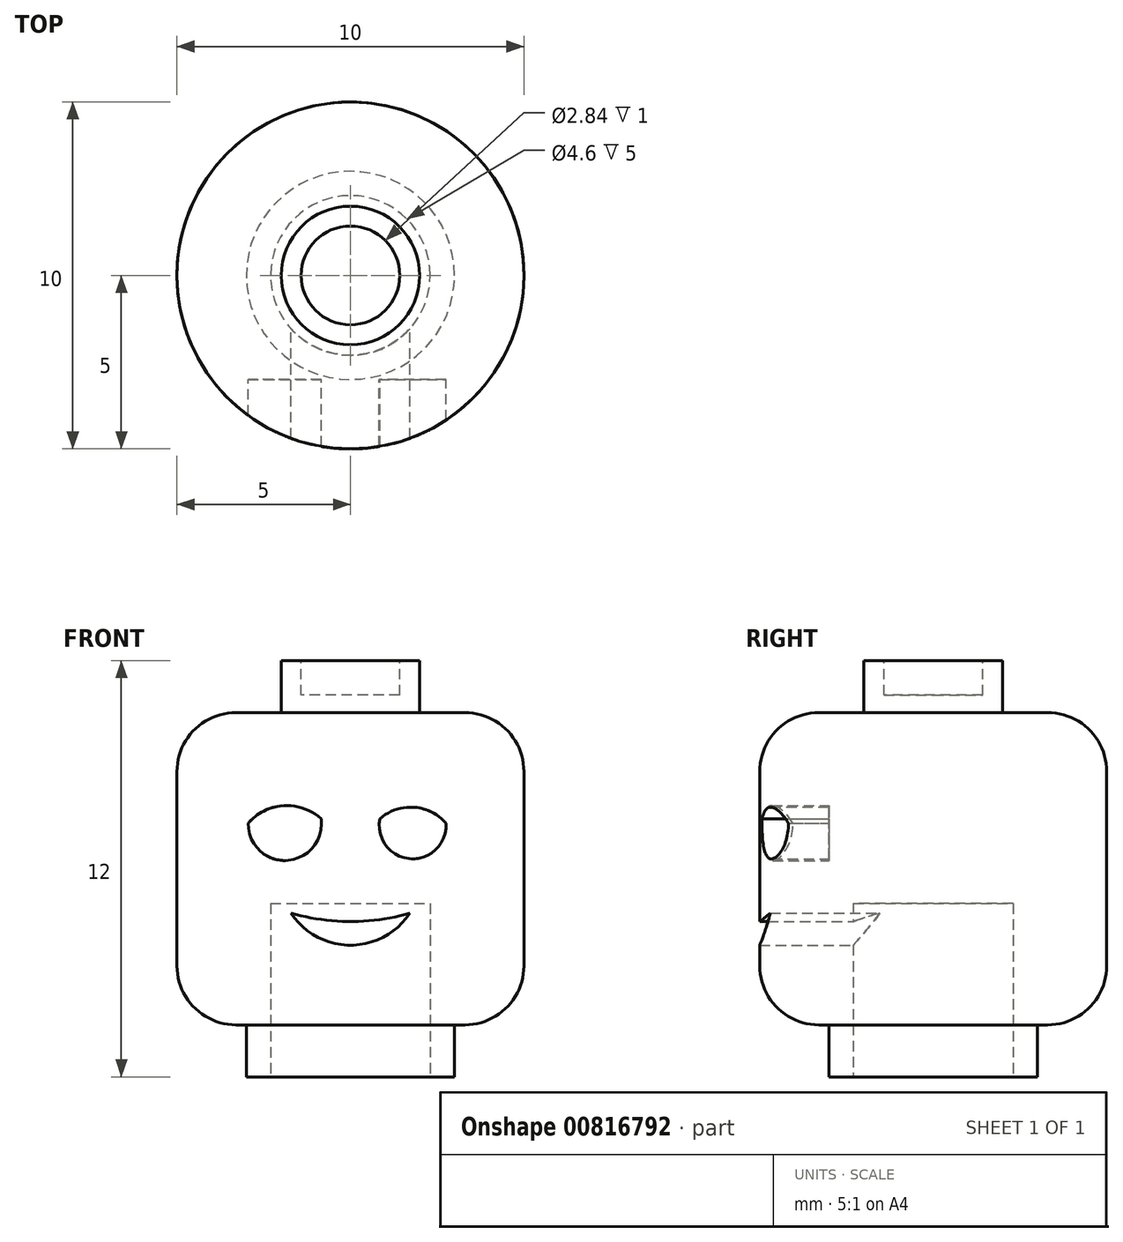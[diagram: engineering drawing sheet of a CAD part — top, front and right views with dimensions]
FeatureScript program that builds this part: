
annotation { "Feature Type Name" : "Feature", "Feature Type Description" : "" }
export const myFeature = defineFeature(function(context is Context, id is Id, definition is map)
    precondition{}
    {
        {
            var Q0;
            Q0=qCreatedBy(makeId("Top.planeOp"),FACE);
            var sketch = newSketch(context, id + "F0", { "sketchPlane" : qUnion([Q0])});
            skCircle(sketch, "E0", {"center": v(0, 0) * mm, "radius": 3 * mm});
            skSolve(sketch);
        }
        {
            var Q0;
            Q0 = qSketchRegion(id + "F0", true);
            extrude(context, id + "F1", {"entities" : qUnion([Q0]), "oppositeDirection" : true, "depth" : 12 * mm, "offsetDistance" : 25 * mm});
        }
        {
            var Q0;
            Q0=makeQuery(id+"F1.opExtrude","CAP_FACE",FACE,{"disambiguationData":[OSD([sQuery(id+"F0.wireOp",EDGE,"E0")])],"isStart":true});
            var sketch = newSketch(context, id + "F2", { "sketchPlane" : qUnion([Q0])});
            skCircle(sketch, "E1", {"center": v(0, 0) * mm, "radius": 2 * mm});
            skCircle(sketch, "E2", {"center": v(0, 0) * mm, "radius": 3.2 * mm});
            skSolve(sketch);
        }
        {
            var Q0;
            Q0 = qSketchRegion(id + "F2", true);
            extrude(context, id + "F3", {"entities" : qUnion([Q0]), "operationType" : NewBodyOperationType.REMOVE, "oppositeDirection" : true, "depth" : 1.5 * mm, "offsetDistance" : 25 * mm});
        }
        {
            var Q0;
            Q0=makeQuery(id+"F3.boolean.opBoolean","COPY",FACE,{"derivedFrom":makeQuery(id+"F3.opExtrude","CAP_FACE",FACE,{"disambiguationData":[OSD([sQuery(id+"F2.wireOp",EDGE,"E1"),sQuery(id+"F2.wireOp",EDGE,"E2")])],"isStart":false})});
            var sketch = newSketch(context, id + "F4", { "sketchPlane" : qUnion([Q0])});
            skCircle(sketch, "E3", {"center": v(0, 0) * mm, "radius": 5 * mm});
            skSolve(sketch);
        }
        {
            var Q0;
            Q0 = qSketchRegion(id + "F4", true);
            extrude(context, id + "F5", {"entities" : qUnion([Q0]), "operationType" : NewBodyOperationType.ADD, "oppositeDirection" : true, "depth" : 9 * mm, "offsetDistance" : 25 * mm});
        }
        {
            var Q0;
            Q0=makeQuery(id+"F5.opExtrude","SWEPT_FACE",FACE,{"disambiguationData":[OSD([sQuery(id+"F4.wireOp",EDGE,"E3")])]});
            fillet(context, id + "F6", {"entities" : qUnion([Q0]), "radius" : 1.7 * mm, "tangentPropagation" : true, "allowEdgeOverflow" : false});
        }
        {
            var Q0;
            Q0=makeQuery(id+"F1.opExtrude","CAP_FACE",FACE,{"disambiguationData":[OSD([sQuery(id+"F0.wireOp",EDGE,"E0")])],"isStart":true});
            var sketch = newSketch(context, id + "F7", { "sketchPlane" : qUnion([Q0])});
            skCircle(sketch, "E4", {"center": v(0, 0) * mm, "radius": 1.42 * mm});
            skSolve(sketch);
        }
        {
            var Q0;
            Q0 = qSketchRegion(id + "F7", true);
            extrude(context, id + "F8", {"entities" : qUnion([Q0]), "operationType" : NewBodyOperationType.REMOVE, "oppositeDirection" : true, "depth" : 1 * mm, "offsetDistance" : 25 * mm});
        }
        {
            var Q0;
            Q0=makeQuery(id+"F1.opExtrude","CAP_FACE",FACE,{"disambiguationData":[OSD([sQuery(id+"F0.wireOp",EDGE,"E0")])],"isStart":false});
            var sketch = newSketch(context, id + "F9", { "sketchPlane" : qUnion([Q0])});
            skCircle(sketch, "E5", {"center": v(0, 0) * mm, "radius": 2.3 * mm});
            skSolve(sketch);
        }
        {
            var Q0;
            Q0 = qSketchRegion(id + "F9", true);
            extrude(context, id + "F10", {"entities" : qUnion([Q0]), "operationType" : NewBodyOperationType.REMOVE, "oppositeDirection" : true, "depth" : 5 * mm, "offsetDistance" : 25 * mm});
        }
        {
            var Q0;
            Q0=qCreatedBy(makeId("Front.planeOp"),FACE);
            var sketch = newSketch(context, id + "F11", { "sketchPlane" : qUnion([Q0])});
            skArc(sketch, "E6", {"start": v(-1.72, -7.28) * mm, "mid": v(0, -8.2) * mm, "end": v(1.7, -7.28) * mm});
            skArc(sketch, "E7", {"start": v(-1.72, -7.28) * mm, "mid": v(0, -7.52) * mm, "end": v(1.7, -7.28) * mm});
            skArc(sketch, "E8", {"start": v(-0.84, -4.56) * mm, "mid": v(-1.92, -4.18) * mm, "end": v(-2.95, -4.69) * mm});
            skArc(sketch, "E9", {"start": v(-2.95, -4.69) * mm, "mid": v(-1.82, -5.76) * mm, "end": v(-0.84, -4.56) * mm});
            skArc(sketch, "E10", {"start": v(2.75, -4.69) * mm, "mid": v(1.83, -4.23) * mm, "end": v(0.85, -4.56) * mm});
            skArc(sketch, "E11", {"start": v(0.85, -4.56) * mm, "mid": v(1.72, -5.72) * mm, "end": v(2.75, -4.69) * mm});
            skSolve(sketch);
        }
        {
            var Q0;
            Q0 = qSketchRegion(id + "F11", true);
            extrude(context, id + "F12", {"entities" : qUnion([Q0]), "operationType" : NewBodyOperationType.REMOVE, "depth" : 25 * mm, "offsetDistance" : 25 * mm});
        }
        {
            var Q0;
            Q0=makeQuery(id+"F12.boolean.opBoolean","COPY",FACE,{"derivedFrom":makeQuery(id+"F12.opExtrude","CAP_FACE",FACE,{"disambiguationData":[OSD([sQuery(id+"F11.wireOp",EDGE,"E8"),sQuery(id+"F11.wireOp",EDGE,"E9")])],"isStart":true})});
            var Q1;
            Q1=makeQuery(id+"F12.boolean.opBoolean","COPY",FACE,{"derivedFrom":makeQuery(id+"F12.opExtrude","CAP_FACE",FACE,{"disambiguationData":[OSD([sQuery(id+"F11.wireOp",EDGE,"E10"),sQuery(id+"F11.wireOp",EDGE,"E11")])],"isStart":true})});
            extrude(context, id + "F13", {"entities" : qUnion([Q0, Q1]), "operationType" : NewBodyOperationType.ADD, "depth" : 3 * mm, "offsetDistance" : 25 * mm});
        }
    });
